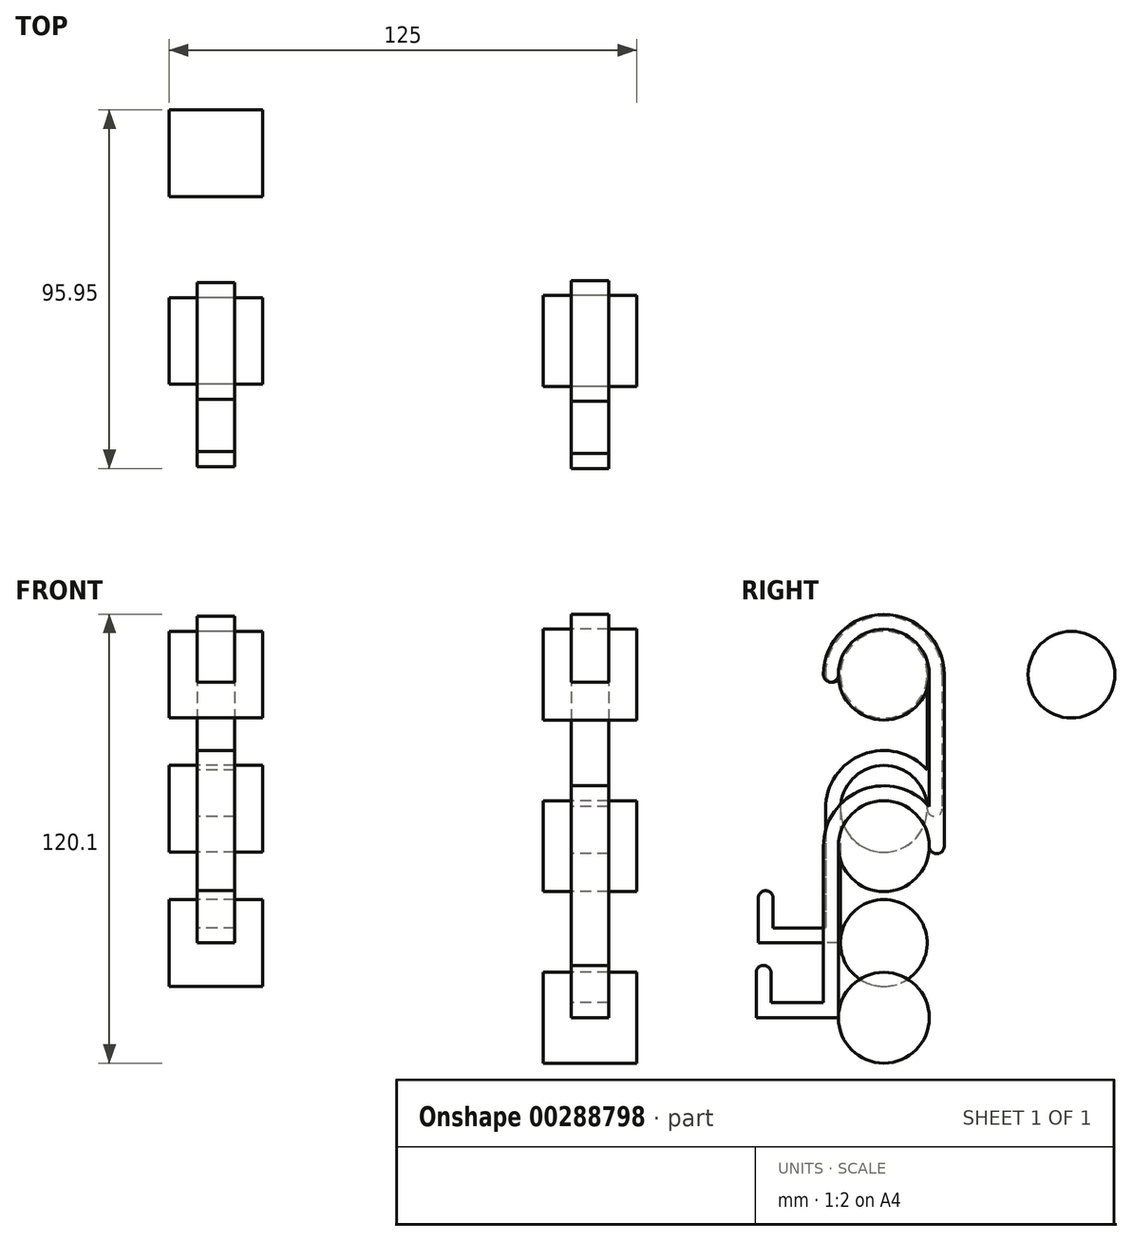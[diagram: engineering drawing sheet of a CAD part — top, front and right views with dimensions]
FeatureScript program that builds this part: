
annotation { "Feature Type Name" : "Feature", "Feature Type Description" : "" }
export const myFeature = defineFeature(function(context is Context, id is Id, definition is map)
    precondition{}
    {
        {
            var Q0;
            Q0=qCreatedBy(makeId("Right.planeOp"),FACE);
            var sketch = newSketch(context, id + "F0", { "sketchPlane" : qUnion([Q0])});
            skCircle(sketch, "E0", {"center": v(0, 0) * mm, "radius": 11.6 * mm});
            skLineSegment(sketch, "E1", {"start": v(0, -11.6) * mm, "end": v(0, -24.3) * mm, "construction": true});
            skLineSegment(sketch, "E2", {"start": v(0, -24.3) * mm, "end": v(0, -47.5) * mm, "construction": true});
            skLineSegment(sketch, "E3", {"start": v(11.6, 0) * mm, "end": v(11.6, -35.9) * mm, "construction": true});
            skCircle(sketch, "E4", {"center": v(0, -35.9) * mm, "radius": 11.6 * mm});
            skLineSegment(sketch, "E5", {"start": v(11.6, 0) * mm, "end": v(38.6, 0) * mm, "construction": true});
            skLineSegment(sketch, "E6", {"start": v(0, 11.6) * mm, "end": v(50.2, 11.6) * mm, "construction": true});
            skLineSegment(sketch, "E7", {"start": v(38.6, 0) * mm, "end": v(61.8, 0) * mm, "construction": true});
            skCircle(sketch, "E8", {"center": v(50.2, 0) * mm, "radius": 11.6 * mm});
            skSolve(sketch);
        }
        {
            var Q0;
            Q0=makeQuery(id+"F0.imprint","IMPRINT",FACE,{"disambiguationData":[TD([[makeQuery(id+"F0.imprint","IMPRINT",EDGE,{"derivedFrom":sQuery(id+"F0.wireOp",EDGE,"E0")}),1.0]])]});
            var Q1;
            Q1=makeQuery(id+"F0.imprint","IMPRINT",FACE,{"disambiguationData":[TD([[makeQuery(id+"F0.imprint","IMPRINT",EDGE,{"derivedFrom":sQuery(id+"F0.wireOp",EDGE,"E4")}),1.0]])]});
            var Q2;
            Q2=makeQuery(id+"F0.imprint","IMPRINT",FACE,{"disambiguationData":[TD([[makeQuery(id+"F0.imprint","IMPRINT",EDGE,{"derivedFrom":sQuery(id+"F0.wireOp",EDGE,"E8")}),1.0]])]});
            extrude(context, id + "F1", {"entities" : qUnion([Q0, Q1, Q2]), "depth" : 25 * mm, "symmetric" : true});
        }
        {
            var Q0;
            Q0=qCreatedBy(makeId("Right.planeOp"),FACE);
            var sketch = newSketch(context, id + "F2", { "sketchPlane" : qUnion([Q0])});
            skArc(sketch, "E9.0", {"start": v(11.6, 0) * mm, "mid": v(0, 11.6) * mm, "end": v(-11.6, 0) * mm});
            skCircle(sketch, "E10.0", {"center": v(0, -35.9) * mm, "radius": 11.6 * mm});
            skLineSegment(sketch, "E11", {"start": v(0, 11.6) * mm, "end": v(0, 15.6) * mm, "construction": true});
            skPoint(sketch, "E11.endSnap0", {"position": v(0, 11.6) * mm});
            skLineSegment(sketch, "E12", {"start": v(0, 11.6) * mm, "end": v(0, -24.3) * mm, "construction": true});
            skLineSegment(sketch, "E13", {"start": v(-11.6, 0) * mm, "end": v(-15.6, 0) * mm, "construction": true});
            skLineSegment(sketch, "E14", {"start": v(11.6, 0) * mm, "end": v(15.6, 0) * mm, "construction": true});
            skArc(sketch, "E15", {"start": v(15.6, 0) * mm, "mid": v(0, 15.6) * mm, "end": v(-15.6, 0) * mm});
            skLineSegment(sketch, "E16", {"start": v(11.6, 0) * mm, "end": v(11.6, -25.47) * mm});
            skLineSegment(sketch, "E17", {"start": v(15.6, 0) * mm, "end": v(15.6, -35.9) * mm});
            skLineSegment(sketch, "E18", {"start": v(-11.6, -35.9) * mm, "end": v(-15.6, -35.9) * mm, "construction": true});
            skLineSegment(sketch, "E19", {"start": v(0, -24.3) * mm, "end": v(0, -20.3) * mm, "construction": true});
            skArc(sketch, "E20", {"start": v(11.6, -25.47) * mm, "mid": v(-5.59, -21.33) * mm, "end": v(-15.6, -35.9) * mm});
            skLineSegment(sketch, "E21", {"start": v(0, -47.5) * mm, "end": v(0, -60.2) * mm, "construction": true});
            skLineSegment(sketch, "E22", {"start": v(0, -60.2) * mm, "end": v(0, -83.4) * mm, "construction": true});
            skLineSegment(sketch, "E23", {"start": v(-11.6, -35.9) * mm, "end": v(-11.6, -71.8) * mm});
            skCircle(sketch, "E24", {"center": v(0, -71.8) * mm, "radius": 11.6 * mm});
            skLineSegment(sketch, "E25", {"start": v(-15.6, -35.9) * mm, "end": v(-15.6, -67.8) * mm});
            skLineSegment(sketch, "E26", {"start": v(-11.6, -71.8) * mm, "end": v(-33.6, -71.8) * mm});
            skLineSegment(sketch, "E27", {"start": v(-33.6, -71.8) * mm, "end": v(-33.6, -59.8) * mm});
            skLineSegment(sketch, "E28", {"start": v(-33.6, -59.8) * mm, "end": v(-29.6, -59.8) * mm, "construction": true});
            skLineSegment(sketch, "E29", {"start": v(-29.6, -59.8) * mm, "end": v(-29.6, -67.8) * mm});
            skLineSegment(sketch, "E30", {"start": v(-15.6, -67.8) * mm, "end": v(-29.6, -67.8) * mm});
            skPoint(sketch, "E31.orphan", {"position": v(-15.6, -71.8) * mm});
            skLineSegment(sketch, "E32", {"start": v(11.6, -35.9) * mm, "end": v(15.6, -35.9) * mm, "construction": true});
            skArc(sketch, "E33", {"start": v(11.6, -35.9) * mm, "mid": v(13.6, -37.9) * mm, "end": v(15.6, -35.9) * mm});
            skArc(sketch, "E34", {"start": v(-15.6, 0) * mm, "mid": v(-13.6, -2) * mm, "end": v(-11.6, 0) * mm});
            skArc(sketch, "E35", {"start": v(-29.6, -59.8) * mm, "mid": v(-31.6, -57.8) * mm, "end": v(-33.6, -59.8) * mm});
            skPoint(sketch, "E36", {"position": v(11.6, -25.47) * mm});
            skSolve(sketch);
        }
        {
            var Q0;
            Q0=makeQuery(id+"F2.imprint","IMPRINT",FACE,{"disambiguationData":[TD([[makeQuery(id+"F2.imprint","IMPRINT",EDGE,{"derivedFrom":sQuery(id+"F2.wireOp",EDGE,"E9.0")}),-1.0]])]});
            extrude(context, id + "F3", {"entities" : qUnion([Q0]), "depth" : 10 * mm, "symmetric" : true});
        }
        {
            var Q0;
            Q0=makeQuery(id+"F2.imprint","IMPRINT",FACE,{"disambiguationData":[TD([[makeQuery(id+"F2.imprint","IMPRINT",EDGE,{"derivedFrom":sQuery(id+"F2.wireOp",EDGE,"E24")}),1.0]])]});
            extrude(context, id + "F4", {"entities" : qUnion([Q0]), "depth" : 25 * mm, "symmetric" : true});
        }
        {
            var Q0;
            Q0=qCreatedBy(makeId("Right.planeOp"),FACE);
            cPlane(context, id + "F5", {"entities" : qUnion([Q0]), "cplaneType" : CPlaneType.OFFSET, "offset" : 100 * mm, "width" : 150 * mm, "height" : 150 * mm});
        }
        {
            var Q0;
            Q0=qCreatedBy(id+"F5.planeOp",FACE);
            var sketch = newSketch(context, id + "F6", { "sketchPlane" : qUnion([Q0])});
            skCircle(sketch, "E37", {"center": v(0, 0) * mm, "radius": 12.15 * mm});
            skLineSegment(sketch, "E38", {"start": v(0, -12.15) * mm, "end": v(0, -33.75) * mm, "construction": true});
            skLineSegment(sketch, "E39", {"start": v(0, -33.75) * mm, "end": v(0, -58.05) * mm, "construction": true});
            skLineSegment(sketch, "E40", {"start": v(12.15, 0) * mm, "end": v(12.15, -35.26) * mm});
            skCircle(sketch, "E41", {"center": v(0, -45.9) * mm, "radius": 12.15 * mm});
            skLineSegment(sketch, "E42", {"start": v(0, 0) * mm, "end": v(0, 12.15) * mm, "construction": true});
            skLineSegment(sketch, "E43", {"start": v(12.15, 0) * mm, "end": v(0, 0) * mm, "construction": true});
            skLineSegment(sketch, "E44", {"start": v(0, -45.9) * mm, "end": v(12.15, -45.9) * mm, "construction": true});
            skLineSegment(sketch, "E45", {"start": v(0, -58.05) * mm, "end": v(0, -79.65) * mm, "construction": true});
            skLineSegment(sketch, "E46", {"start": v(0, -79.65) * mm, "end": v(0, -103.95) * mm, "construction": true});
            skLineSegment(sketch, "E47", {"start": v(12.15, -45.9) * mm, "end": v(12.15, -91.8) * mm, "construction": true});
            skCircle(sketch, "E48", {"center": v(0, -91.8) * mm, "radius": 12.15 * mm});
            skLineSegment(sketch, "E49", {"start": v(0, -91.8) * mm, "end": v(12.15, -91.8) * mm, "construction": true});
            skLineSegment(sketch, "E50", {"start": v(-12.15, 0) * mm, "end": v(-16.15, 0) * mm, "construction": true});
            skLineSegment(sketch, "E51", {"start": v(12.15, 0) * mm, "end": v(16.15, 0) * mm, "construction": true});
            skLineSegment(sketch, "E52", {"start": v(0, 12.15) * mm, "end": v(0, 16.15) * mm, "construction": true});
            skArc(sketch, "E53", {"start": v(16.15, 0) * mm, "mid": v(0, 16.15) * mm, "end": v(-16.15, 0) * mm});
            skLineSegment(sketch, "E54", {"start": v(16.15, 0) * mm, "end": v(16.15, -45.9) * mm});
            skLineSegment(sketch, "E55", {"start": v(-12.15, -45.9) * mm, "end": v(-16.15, -45.9) * mm, "construction": true});
            skLineSegment(sketch, "E56", {"start": v(0, -33.75) * mm, "end": v(0, -29.75) * mm, "construction": true});
            skArc(sketch, "E57", {"start": v(12.15, -35.26) * mm, "mid": v(-5.68, -30.78) * mm, "end": v(-16.15, -45.9) * mm});
            skLineSegment(sketch, "E58", {"start": v(-12.15, -45.9) * mm, "end": v(-12.15, -91.8) * mm});
            skLineSegment(sketch, "E59", {"start": v(-12.15, -91.8) * mm, "end": v(-34.15, -91.8) * mm});
            skLineSegment(sketch, "E60", {"start": v(-34.15, -91.8) * mm, "end": v(-34.15, -79.8) * mm});
            skLineSegment(sketch, "E61", {"start": v(-34.15, -79.8) * mm, "end": v(-30.15, -79.8) * mm, "construction": true});
            skLineSegment(sketch, "E62", {"start": v(-30.15, -79.8) * mm, "end": v(-30.15, -87.8) * mm});
            skLineSegment(sketch, "E63", {"start": v(-16.15, -45.9) * mm, "end": v(-16.15, -87.8) * mm});
            skLineSegment(sketch, "E64", {"start": v(-16.15, -87.8) * mm, "end": v(-30.15, -87.8) * mm});
            skLineSegment(sketch, "E65", {"start": v(12.15, -45.9) * mm, "end": v(16.15, -45.9) * mm, "construction": true});
            skArc(sketch, "E66", {"start": v(-16.15, 0) * mm, "mid": v(-14.15, -2) * mm, "end": v(-12.15, 0) * mm});
            skArc(sketch, "E67", {"start": v(12.15, -45.9) * mm, "mid": v(14.15, -47.9) * mm, "end": v(16.15, -45.9) * mm});
            skArc(sketch, "E68", {"start": v(-30.15, -79.8) * mm, "mid": v(-32.15, -77.8) * mm, "end": v(-34.15, -79.8) * mm});
            skSolve(sketch);
        }
        {
            var Q0;
            {var subQ0=sQuery(id+"F6.wireOp",EDGE,"E37");var subQ1=makeQuery(id+"F6.imprint","INTERSECT",VERTEX,{"derivedFrom":[subQ0,sQuery(id+"F6.wireOp",EDGE,"E40")]});Q0=makeQuery(id+"F6.imprint","IMPRINT",FACE,{"disambiguationData":[TD([[makeQuery(id+"F6.imprint","IMPRINT",EDGE,{"disambiguationData":[TD([[subQ1,-1.0]])],"derivedFrom":subQ0}),1.0]])]});}
            var Q1;
            {var subQ0=sQuery(id+"F6.wireOp",EDGE,"E41");var subQ1=makeQuery(id+"F6.imprint","INTERSECT",VERTEX,{"derivedFrom":[subQ0,sQuery(id+"F6.wireOp",EDGE,"E58")]});Q1=makeQuery(id+"F6.imprint","IMPRINT",FACE,{"disambiguationData":[TD([[makeQuery(id+"F6.imprint","IMPRINT",EDGE,{"disambiguationData":[TD([[subQ1,1.0]])],"derivedFrom":subQ0}),1.0]])]});}
            var Q2;
            Q2=makeQuery(id+"F6.imprint","IMPRINT",FACE,{"disambiguationData":[TD([[makeQuery(id+"F6.imprint","IMPRINT",EDGE,{"derivedFrom":sQuery(id+"F6.wireOp",EDGE,"E48")}),1.0]])]});
            extrude(context, id + "F7", {"entities" : qUnion([Q0, Q1, Q2]), "depth" : 25 * mm, "symmetric" : true});
        }
        {
            var Q0;
            {var subQ1=sQuery(id+"F6.wireOp",EDGE,"E40");Q0=makeQuery(id+"F6.imprint","IMPRINT",FACE,{"disambiguationData":[TD([[makeQuery(id+"F6.imprint","IMPRINT",EDGE,{"derivedFrom":subQ1}),1.0]])]});}
            extrude(context, id + "F8", {"entities" : qUnion([Q0]), "depth" : 10 * mm, "symmetric" : true});
        }
    });
